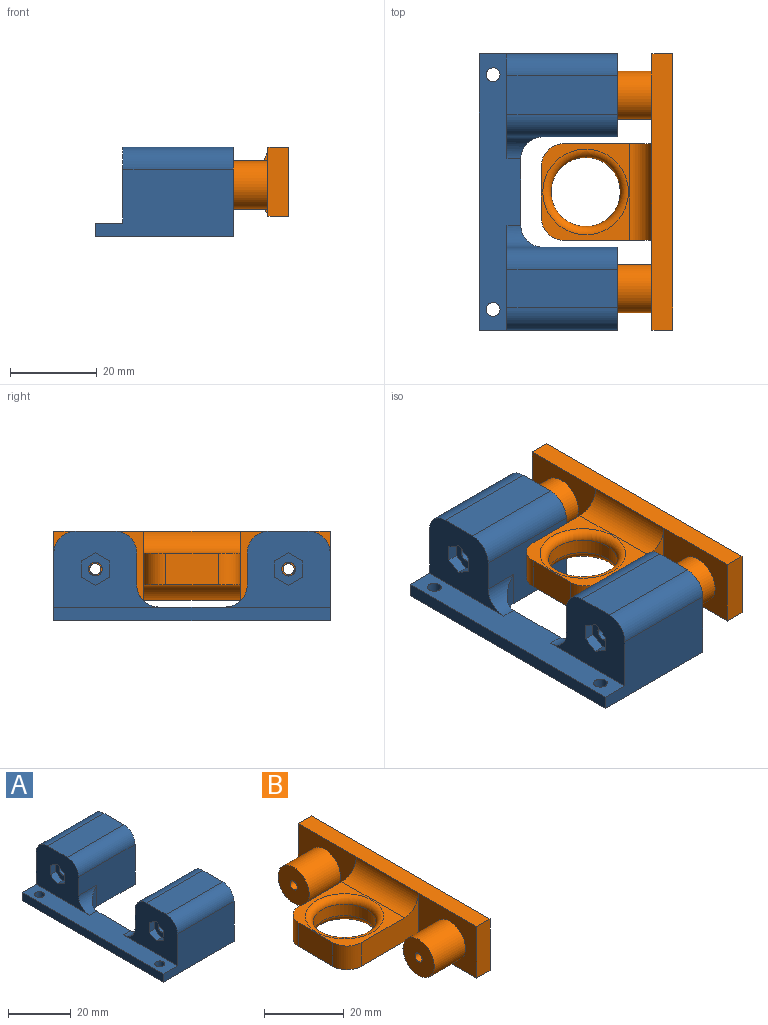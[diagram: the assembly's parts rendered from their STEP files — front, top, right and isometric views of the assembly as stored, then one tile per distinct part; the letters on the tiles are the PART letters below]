
ASSEMBLY  parts=2 mates=1
PART A: 44 faces, bbox 31.8x63.5x20.6 mm
  f0: plane 24.13x17.46mm, normal (-1,0,0), area 290.8mm2, adj f5,f10,f11,f16,f21,f28,f29,f30
  f1: plane 24.13x17.46mm, normal (-1,0,0), area 290.8mm2, adj f5,f6,f8,f17,f20,f26,f27,f38
  f2: cylinder r=1.59mm len=3.18mm, axis (1,0,0), area 23.8mm2, adj f25,f37
  f3: cylinder r=1.59mm len=3.18mm, axis (1,0,0), area 23.8mm2, adj f23,f36
  f4: plane 20.64x19.05mm, normal (1,0,0), area 255.4mm2, adj f10,f11,f15,f16,f22,f28,f29
  f5: plane 63.5x9.53mm, normal (0,0,1), area 435.8mm2, adj f0,f1,f6,f9,f11,f12,f13,f14
  f6: plane 31.75x15.56mm, normal (0,-1,0), area 415.3mm2, adj f1,f5,f7,f13,f15,f27
  f7: plane 20.64x19.05mm, normal (1,0,0), area 255.4mm2, adj f6,f8,f15,f17,f24,f26,f27
  f8: plane 25.4x15.56mm, normal (0,1,0), area 327mm2, adj f1,f7,f15,f18,f20,f26
  f9: plane 15.24x3.18mm, normal (1,0,0), area 48.4mm2, adj f5,f15,f18,f19
  f10: plane 25.4x15.56mm, normal (0,-1,0), area 327mm2, adj f0,f4,f15,f19,f21,f28
  f11: plane 31.75x15.56mm, normal (0,1,0), area 415.3mm2, adj f0,f4,f5,f13,f15,f29
  f12: cylinder r=1.59mm len=3.18mm, axis (0,0,-1), area 31.7mm2, adj f5,f15
  f13: plane 63.5x3.18mm, normal (-1,0,0), area 201.6mm2, adj f5,f6,f11,f15
  f14: cylinder r=1.59mm len=3.18mm, axis (0,0,-1), area 31.7mm2, adj f5,f15
  f15: plane 63.5x31.75mm, normal (0,0,-1), area 1446.9mm2, adj f4,f6,f7,f8,f9,f10,f11,f12
  f16: plane 25.4x8.89mm, normal (0,0,1), area 225.8mm2, adj f0,f4,f28,f29
  f17: plane 25.4x8.89mm, normal (0,0,1), area 225.8mm2, adj f1,f7,f26,f27
  f18: cylinder r=5.08mm len=8.26mm, axis (0,0,-1), area 40.1mm2, adj f8,f9,f15,f20
  f19: cylinder r=5.08mm len=8.26mm, axis (0,0,1), area 40.1mm2, adj f9,f10,f15,f21
  f20: cylinder r=5.08mm len=8.26mm, axis (1,0,0), area 40.1mm2, adj f1,f5,f8,f18
  f21: cylinder r=5.08mm len=8.26mm, axis (-1,0,0), area 40.1mm2, adj f0,f5,f10,f19
  f22: cylinder r=6.35mm len=20.64mm, axis (1,0,0), area 823.4mm2, adj f4,f23
  f23: plane 12.7x12.7mm, normal (1,0,0), area 118.8mm2, adj f3,f22
  f24: cylinder r=6.35mm len=20.64mm, axis (1,0,0), area 823.4mm2, adj f7,f25
  f25: plane 12.7x12.7mm, normal (1,0,0), area 118.8mm2, adj f2,f24
  f26: cylinder r=5.08mm len=25.4mm, axis (1,0,0), area 202.7mm2, adj f1,f7,f8,f17
  f27: cylinder r=5.08mm len=25.4mm, axis (-1,0,0), area 202.7mm2, adj f1,f6,f7,f17
  f28: cylinder r=5.08mm len=25.4mm, axis (-1,0,0), area 202.7mm2, adj f0,f4,f10,f16
  f29: cylinder r=5.08mm len=25.4mm, axis (1,0,0), area 202.7mm2, adj f0,f4,f11,f16
  f30: plane 3.74x2.38mm, normal (0,1,0), area 8.9mm2, adj f0,f31,f35,f36
  f31: plane 3.24x2.38mm, normal (0,0.5,-0.87), area 8.9mm2, adj f0,f30,f32,f36
  f32: plane 3.24x2.38mm, normal (0,-0.5,-0.87), area 8.9mm2, adj f0,f31,f33,f36
  f33: plane 3.74x2.38mm, normal (0,-1,0), area 8.9mm2, adj f0,f32,f34,f36
  f34: plane 3.24x2.38mm, normal (0,-0.5,0.87), area 8.9mm2, adj f0,f33,f35,f36
  f35: plane 3.24x2.38mm, normal (0,0.5,0.87), area 8.9mm2, adj f0,f30,f34,f36
  f36: plane 7.48x6.48mm, normal (-1,0,0), area 28.4mm2, adj f3,f30,f31,f32,f33,f34,f35
  f37: plane 7.48x6.48mm, normal (-1,0,0), area 28.4mm2, adj f2,f38,f39,f40,f41,f42,f43
  f38: plane 3.24x2.38mm, normal (0,0.5,-0.87), area 8.9mm2, adj f1,f37,f39,f43
  f39: plane 3.24x2.38mm, normal (0,-0.5,-0.87), area 8.9mm2, adj f1,f37,f38,f40
  f40: plane 3.74x2.38mm, normal (0,-1,0), area 8.9mm2, adj f1,f37,f39,f41
  f41: plane 3.24x2.38mm, normal (0,-0.5,0.87), area 8.9mm2, adj f1,f37,f40,f42
  f42: plane 3.24x2.38mm, normal (0,0.5,0.87), area 8.9mm2, adj f1,f37,f41,f43
  f43: plane 3.74x2.38mm, normal (0,1,0), area 8.9mm2, adj f1,f37,f38,f42
PART B: 29 faces, bbox 32.1x63.5x15.9 mm
  f0: cylinder r=1.27mm len=6.35mm, axis (-1,0,0), area 50.7mm2, adj f12,f26
  f1: cylinder r=1.27mm len=6.35mm, axis (-1,0,0), area 50.7mm2, adj f10,f28
  f2: plane 20.64x15.88mm, normal (-1,0,0), area 230.6mm2, adj f4,f5,f6,f11,f15
  f3: plane 20.64x15.88mm, normal (-1,0,0), area 230.6mm2, adj f4,f6,f7,f9,f13
  f4: plane 63.5x4.76mm, normal (0,0,-1), area 302.4mm2, adj f2,f3,f5,f7,f8,f18
  f5: plane 15.88x4.76mm, normal (0,1,0), area 75.6mm2, adj f2,f4,f6,f8
  f6: plane 63.5x4.76mm, normal (0,0,1), area 302.4mm2, adj f2,f3,f5,f7,f8,f19
  f7: plane 15.88x4.76mm, normal (0,-1,0), area 75.6mm2, adj f3,f4,f6,f8
  f8: plane 63.5x15.88mm, normal (1,0,0), area 944.7mm2, adj f4,f5,f6,f7,f25,f27
  f9: cylinder r=5.56mm len=11.11mm, axis (1,0,0), area 387.9mm2, adj f3,f10
  f10: plane 11.11x11.11mm, normal (-1,0,0), area 91.9mm2, adj f1,f9
  f11: cylinder r=5.56mm len=11.11mm, axis (1,0,0), area 387.9mm2, adj f2,f12
  f12: plane 11.11x11.11mm, normal (-1,0,0), area 91.9mm2, adj f0,f11
  f13: plane 20.32x15.88mm, normal (0,-1,0), area 158.4mm2, adj f3,f14,f16,f18,f19,f21
  f14: plane 22.23x20.57mm, normal (0,0,-1), area 141.8mm2, adj f13,f15,f17,f18,f20,f21,f23
  f15: plane 20.32x15.88mm, normal (0,1,0), area 158.4mm2, adj f2,f14,f16,f18,f19,f20
  f16: plane 22.23x20.32mm, normal (0,0,1), area 136.2mm2, adj f13,f15,f17,f19,f20,f21,f24
  f17: plane 12.07x7.3mm, normal (-1,0,0), area 88.1mm2, adj f14,f16,f20,f21
  f18: cylinder r=5.08mm len=22.23mm, axis (0,-1,0), area 141.5mm2, adj f4,f13,f14,f15
  f19: cylinder r=5.08mm len=22.23mm, axis (0,-1,0), area 177.3mm2, adj f6,f13,f15,f16
  f20: cylinder r=5.08mm len=7.3mm, axis (0,0,-1), area 58.3mm2, adj f14,f15,f16,f17
  f21: cylinder r=5.08mm len=7.3mm, axis (0,0,1), area 58.3mm2, adj f13,f14,f16,f17
  f22: cylinder r=7.94mm len=15.88mm, axis (0,0,1), area 174.2mm2, adj f23,f24
  f23: torus R=9.84mm, axis (0,0,-1), area 162.3mm2, adj f14,f22
  f24: torus R=9.84mm, axis (0,0,-1), area 162.3mm2, adj f16,f22
  f25: cylinder r=3.17mm len=9.53mm, axis (1,0,0), area 190mm2, adj f8,f26
  f26: plane 6.35x6.35mm, normal (1,0,0), area 26.6mm2, adj f0,f25
  f27: cylinder r=3.17mm len=9.53mm, axis (1,0,0), area 190mm2, adj f8,f28
  f28: plane 6.35x6.35mm, normal (1,0,0), area 26.6mm2, adj f1,f27
PLACE A t=(-5.28,-22.28,8.72)mm fixed
PLACE B t=(2.66,-22.28,8.72)mm
MATE slider A.f2 <-> B.f9  axis (1,0,0) through (-14.91,-22.51,20.63)mm
